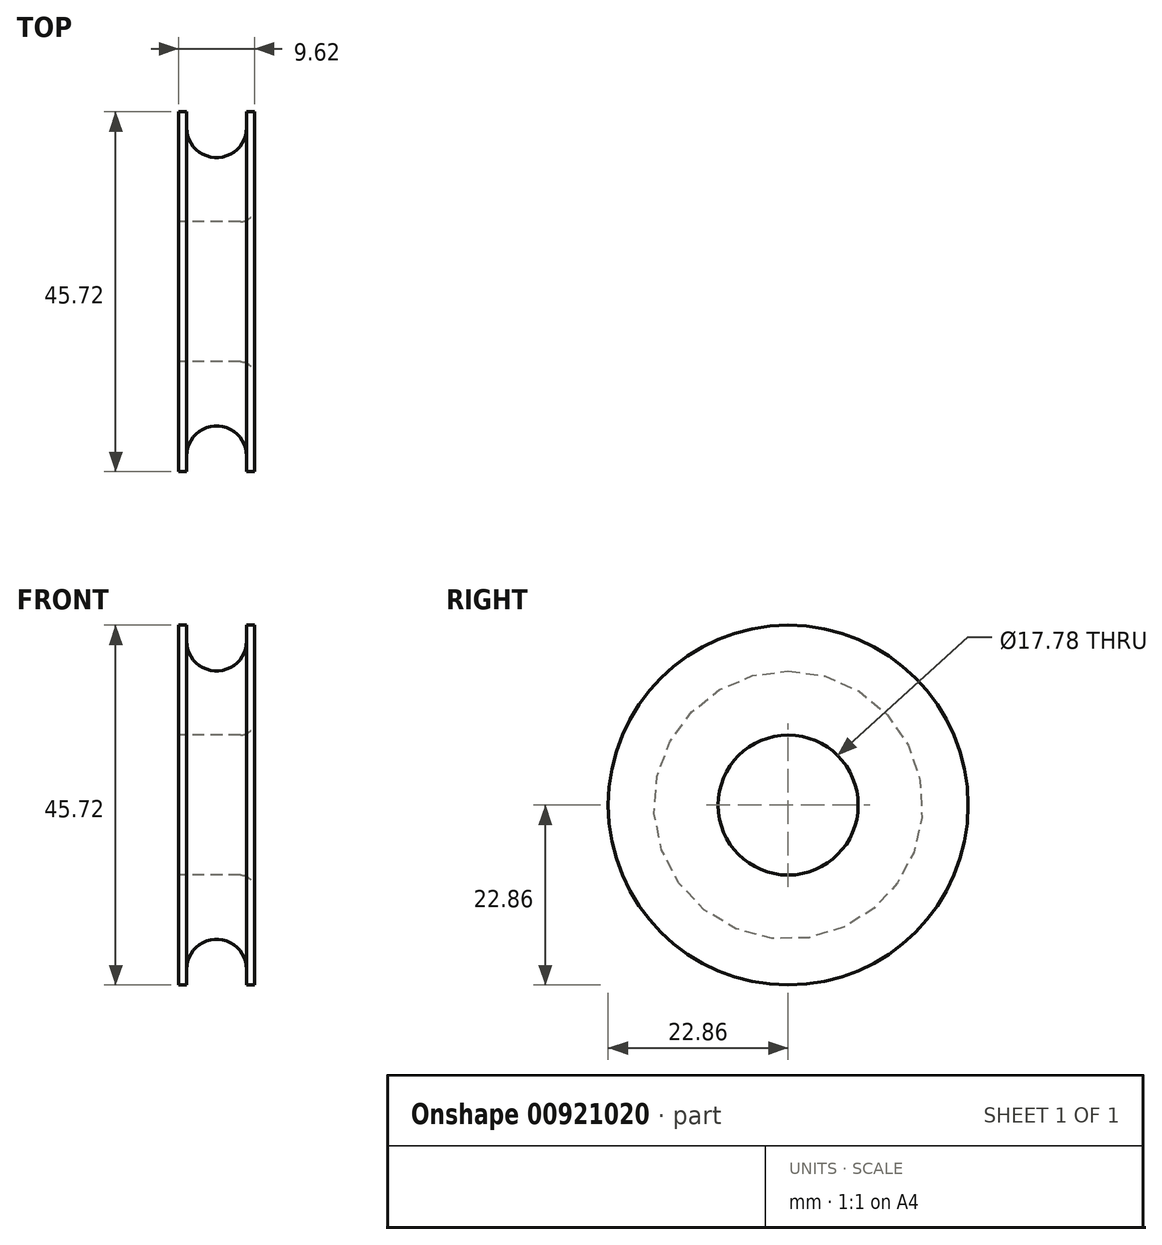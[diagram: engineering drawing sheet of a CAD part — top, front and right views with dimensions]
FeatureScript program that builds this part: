
annotation { "Feature Type Name" : "Feature", "Feature Type Description" : "" }
export const myFeature = defineFeature(function(context is Context, id is Id, definition is map)
    precondition{}
    {
        {
            var Q0;
            Q0=qCreatedBy(makeId("Front.planeOp"),FACE);
            var sketch = newSketch(context, id + "F0", { "sketchPlane" : qUnion([Q0])});
            skLineSegment(sketch, "E0", {"start": v(0, 0) * mm, "end": v(-3.81, 0) * mm});
            skLineSegment(sketch, "E1", {"start": v(-3.81, 0) * mm, "end": v(-3.81, 20.86) * mm});
            skLineSegment(sketch, "E2", {"start": v(3.8, 20.86) * mm, "end": v(3.81, 0) * mm});
            skLineSegment(sketch, "E3", {"start": v(3.81, 0) * mm, "end": v(0, 0) * mm});
            skArc(sketch, "E4", {"start": v(-3.81, 20.86) * mm, "mid": v(0, 17.05) * mm, "end": v(3.8, 20.86) * mm});
            skLineSegment(sketch, "E5", {"start": v(-3.81, 20.86) * mm, "end": v(-3.81, 22.86) * mm});
            skLineSegment(sketch, "E6", {"start": v(3.8, 20.86) * mm, "end": v(3.8, 22.86) * mm});
            skPoint(sketch, "E7", {"position": v(3.8, 20.86) * mm});
            skLineSegment(sketch, "E8", {"start": v(-3.81, 22.86) * mm, "end": v(-4.81, 22.86) * mm});
            skLineSegment(sketch, "E9", {"start": v(-4.81, 22.86) * mm, "end": v(-4.81, 0) * mm});
            skLineSegment(sketch, "E10", {"start": v(-4.81, 0) * mm, "end": v(-3.81, 0) * mm});
            skLineSegment(sketch, "E11", {"start": v(3.81, 0) * mm, "end": v(4.81, 0) * mm});
            skLineSegment(sketch, "E12", {"start": v(4.81, 0) * mm, "end": v(4.81, 22.86) * mm});
            skLineSegment(sketch, "E13", {"start": v(4.81, 22.86) * mm, "end": v(3.8, 22.86) * mm});
            skSolve(sketch);
        }
        {
            var Q0;
            Q0=qCreatedBy(makeId("Top.planeOp"),FACE);
            var sketch = newSketch(context, id + "F1", { "sketchPlane" : qUnion([Q0])});
            skLineSegment(sketch, "E14", {"start": v(-12.1, 0) * mm, "end": v(11.41, 0) * mm});
            skSolve(sketch);
        }
        {
            var Q0;
            Q0=makeQuery(id+"F0.imprint","IMPRINT",FACE,{"disambiguationData":[TD([[makeQuery(id+"F0.imprint","IMPRINT",EDGE,{"derivedFrom":sQuery(id+"F0.wireOp",EDGE,"E0")}),-1.0]])]});
            var Q1;
            Q1=makeQuery(id+"F0.imprint","IMPRINT",FACE,{"disambiguationData":[TD([[makeQuery(id+"F0.imprint","IMPRINT",EDGE,{"derivedFrom":sQuery(id+"F0.wireOp",EDGE,"E1")}),1.0]])]});
            var Q2;
            Q2=makeQuery(id+"F0.imprint","IMPRINT",FACE,{"disambiguationData":[TD([[makeQuery(id+"F0.imprint","IMPRINT",EDGE,{"derivedFrom":sQuery(id+"F0.wireOp",EDGE,"E2")}),1.0]])]});
            var Q3;
            Q3=sQuery(id+"F1.wireOp",EDGE,"E14");
            revolve(context, id + "F2", {"surfaceOperationType" : NewSurfaceOperationType.NEW, "entities" : qUnion([Q0, Q1, Q2]), "axis" : qUnion([Q3]), "revolveType" : RevolveType.FULL});
        }
        {
            var Q0;
            Q0=makeQuery(id+"F2.opRevolve","SWEPT_FACE",FACE,{"disambiguationData":[OSD([sQuery(id+"F0.wireOp",EDGE,"E9")])]});
            var sketch = newSketch(context, id + "F3", { "sketchPlane" : qUnion([Q0])});
            skCircle(sketch, "E15", {"center": v(0, 0) * mm, "radius": 8.9 * mm});
            skSolve(sketch);
        }
        {
            var Q0;
            Q0=makeQuery(id+"F3.imprint","IMPRINT",FACE,{"disambiguationData":[TD([[makeQuery(id+"F3.imprint","IMPRINT",EDGE,{"derivedFrom":sQuery(id+"F3.wireOp",EDGE,"E15")}),1.0]])]});
            extrude(context, id + "F4", {"entities" : qUnion([Q0]), "operationType" : NewBodyOperationType.REMOVE, "oppositeDirection" : true, "depth" : 25.4 * mm, "offsetDistance" : 25.4 * mm});
        }
        {
            var Q0;
            Q0=makeQuery(id+"F4.boolean.opBoolean","INTERSECT",EDGE,{"derivedFrom":[makeQuery(id+"F2.opRevolve","SWEPT_FACE",FACE,{"disambiguationData":[OSD([sQuery(id+"F0.wireOp",EDGE,"E12")])]}),makeQuery(id+"F4.opExtrude","SWEPT_FACE",FACE,{"disambiguationData":[OSD([sQuery(id+"F3.wireOp",EDGE,"E15")])]})]});
            var Q1;
            Q1=makeQuery(id+"F4.boolean.opBoolean","COPY",EDGE,{"derivedFrom":makeQuery(id+"F4.opExtrude","CAP_EDGE",EDGE,{"disambiguationData":[OSD([sQuery(id+"F3.wireOp",EDGE,"E15")])],"isStart":true})});
            fillet(context, id + "F5", {"entities" : qUnion([Q0, Q1]), "radius" : 1.78 * mm, "tangentPropagation" : true, "allowEdgeOverflow" : false});
        }
    });
